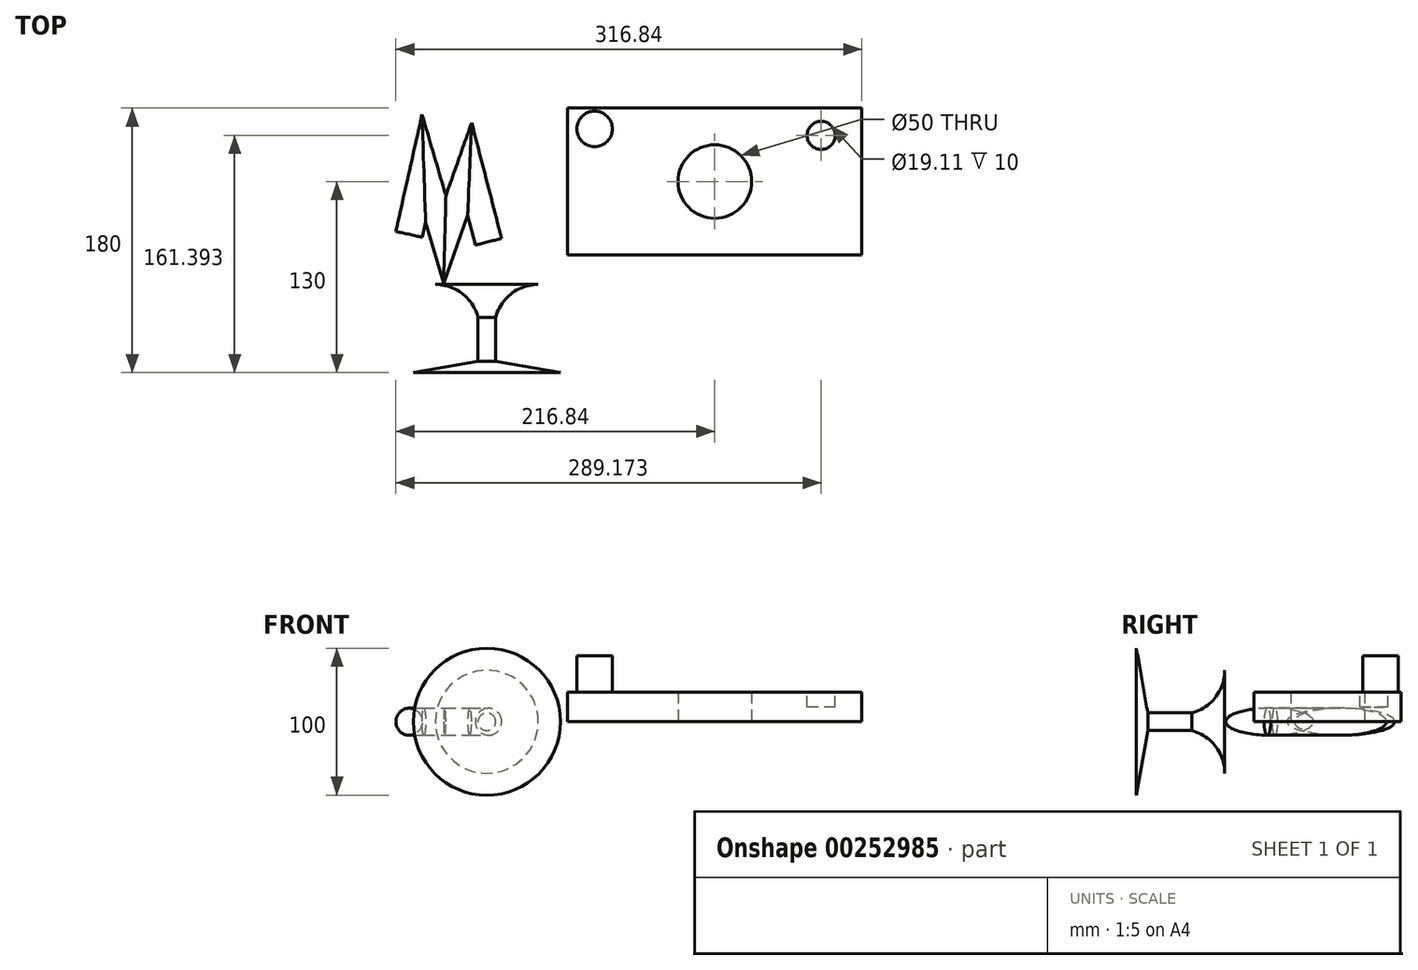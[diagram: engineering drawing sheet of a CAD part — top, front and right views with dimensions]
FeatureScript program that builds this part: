
annotation { "Feature Type Name" : "Feature", "Feature Type Description" : "" }
export const myFeature = defineFeature(function(context is Context, id is Id, definition is map)
    precondition{}
    {
        {
            var Q0;
            Q0=qCreatedBy(makeId("Top.planeOp"),FACE);
            var sketch = newSketch(context, id + "F0", { "sketchPlane" : qUnion([Q0])});
            skLineSegment(sketch, "E0.bottom", {"start": v(0, 100) * mm, "end": v(200, 100) * mm});
            skLineSegment(sketch, "E0.top", {"start": v(0, 0) * mm, "end": v(200, 0) * mm});
            skLineSegment(sketch, "E0.left", {"start": v(0, 100) * mm, "end": v(0, 0) * mm});
            skLineSegment(sketch, "E0.right", {"start": v(200, 100) * mm, "end": v(200, 0) * mm});
            skCircle(sketch, "E1", {"center": v(100, 50) * mm, "radius": 25 * mm});
            skSolve(sketch);
        }
        {
            var Q0;
            Q0=qSketchRegion(id+"F0",true);
            extrude(context, id + "F1", {"entities" : qUnion([Q0]), "depth" : 20 * mm});
        }
        {
            var Q0;
            Q0=makeQuery(id+"F1.opExtrude","CAP_FACE",FACE,{"disambiguationData":[OSD([sQuery(id+"F0.wireOp",EDGE,"E0.bottom"),sQuery(id+"F0.wireOp",EDGE,"E0.top"),sQuery(id+"F0.wireOp",EDGE,"E0.left"),sQuery(id+"F0.wireOp",EDGE,"E0.right"),sQuery(id+"F0.wireOp",EDGE,"E1")])],"isStart":false});
            var sketch = newSketch(context, id + "F2", { "sketchPlane" : qUnion([Q0])});
            skCircle(sketch, "E2", {"center": v(172.33, 81.4) * mm, "radius": 9.56 * mm});
            skSolve(sketch);
        }
        {
            var Q0;
            Q0=makeQuery(id+"F2.imprint","IMPRINT",FACE,{"disambiguationData":[TD([[makeQuery(id+"F2.imprint","IMPRINT",EDGE,{"derivedFrom":sQuery(id+"F2.wireOp",EDGE,"E2")}),1.0]])]});
            extrude(context, id + "F3", {"entities" : qUnion([Q0]), "operationType" : NewBodyOperationType.REMOVE, "oppositeDirection" : true, "depth" : 10 * mm});
        }
        {
            var Q0;
            Q0=makeQuery(id+"F1.opExtrude","CAP_FACE",FACE,{"disambiguationData":[OSD([sQuery(id+"F0.wireOp",EDGE,"E0.bottom"),sQuery(id+"F0.wireOp",EDGE,"E0.top"),sQuery(id+"F0.wireOp",EDGE,"E0.left"),sQuery(id+"F0.wireOp",EDGE,"E0.right"),sQuery(id+"F0.wireOp",EDGE,"E1")])],"isStart":false});
            var sketch = newSketch(context, id + "F4", { "sketchPlane" : qUnion([Q0])});
            skCircle(sketch, "E3", {"center": v(18.3, 85.82) * mm, "radius": 12.11 * mm});
            skSolve(sketch);
        }
        {
            var Q0;
            Q0 = qSketchRegion(id + "F4", true);
            extrude(context, id + "F5", {"entities" : qUnion([Q0]), "operationType" : NewBodyOperationType.ADD, "depth" : 25 * mm});
        }
        {
            var Q0;
            Q0=qCreatedBy(makeId("Top.planeOp"),FACE);
            var sketch = newSketch(context, id + "F6", { "sketchPlane" : qUnion([Q0])});
            skLineSegment(sketch, "E4", {"start": v(-20, -20) * mm, "end": v(-55, -20) * mm});
            skLineSegment(sketch, "E5", {"start": v(-55, -20) * mm, "end": v(-55, -80) * mm});
            skLineSegment(sketch, "E6", {"start": v(-55, -80) * mm, "end": v(-5, -80) * mm});
            skLineSegment(sketch, "E7", {"start": v(-5, -80) * mm, "end": v(-49, -72.32) * mm});
            skLineSegment(sketch, "E8", {"start": v(-49, -72.32) * mm, "end": v(-49, -42.32) * mm});
            skArc(sketch, "E9", {"start": v(-20, -20) * mm, "mid": v(-38.3, -26.23) * mm, "end": v(-49, -42.32) * mm});
            skSolve(sketch);
        }
        {
            var Q0;
            Q0=makeQuery(id+"F6.imprint","IMPRINT",FACE,{"disambiguationData":[TD([[makeQuery(id+"F6.imprint","IMPRINT",EDGE,{"derivedFrom":sQuery(id+"F6.wireOp",EDGE,"E4")}),1.0]])]});
            var Q1;
            Q1=sQuery(id+"F6.wireOp",EDGE,"E5");
            revolve(context, id + "F7", {"entities" : qUnion([Q0]), "axis" : qUnion([Q1]), "revolveType" : RevolveType.FULL});
        }
        {
            var Q0;
            Q0=qCreatedBy(makeId("Top.planeOp"),FACE);
            var sketch = newSketch(context, id + "F8", { "sketchPlane" : qUnion([Q0])});
            skLineSegment(sketch, "E10", {"start": v(-107.36, 13.97) * mm, "end": v(-97.78, 56.83) * mm});
            skLineSegment(sketch, "E11", {"start": v(-97.78, 56.83) * mm, "end": v(-83.68, 8.9) * mm});
            skLineSegment(sketch, "E12", {"start": v(-83.68, 8.9) * mm, "end": v(-66.76, 56.83) * mm});
            skLineSegment(sketch, "E13", {"start": v(-66.76, 56.83) * mm, "end": v(-54.35, 8.9) * mm});
            skSolve(sketch);
        }
        {
            var Q0;
            Q0=sQuery(id+"F8.wireOp",VERTEX,"E10.start");
            var Q1;
            Q1=sQuery(id+"F8.wireOp",EDGE,"E10");
            cPlane(context, id + "F9", {"entities" : qUnion([Q0, Q1]), "cplaneType" : CPlaneType.LINE_POINT, "offset" : 25 * mm, "width" : 150 * mm, "height" : 150 * mm});
        }
        {
            var Q0;
            Q0=qCreatedBy(id+"F9.planeOp",FACE);
            var sketch = newSketch(context, id + "F10", { "sketchPlane" : qUnion([Q0])});
            skCircle(sketch, "E14", {"center": v(108.34, 0) * mm, "radius": 9.2 * mm});
            skSolve(sketch);
        }
        {
            var Q0;
            Q0=makeQuery(id+"F10.imprint","IMPRINT",FACE,{"disambiguationData":[TD([[makeQuery(id+"F10.imprint","IMPRINT",EDGE,{"derivedFrom":sQuery(id+"F10.wireOp",EDGE,"E14")}),1.0]])]});
            var Q1;
            Q1=sQuery(id+"F8.wireOp",EDGE,"E10");
            var Q2;
            Q2=sQuery(id+"F8.wireOp",EDGE,"E11");
            var Q3;
            Q3=sQuery(id+"F8.wireOp",EDGE,"E12");
            var Q4;
            Q4=sQuery(id+"F8.wireOp",EDGE,"E13");
            sweep(context, id + "F11", {"profiles" : qUnion([Q0]), "path" : qUnion([Q1, Q2, Q3, Q4])});
        }
    });
